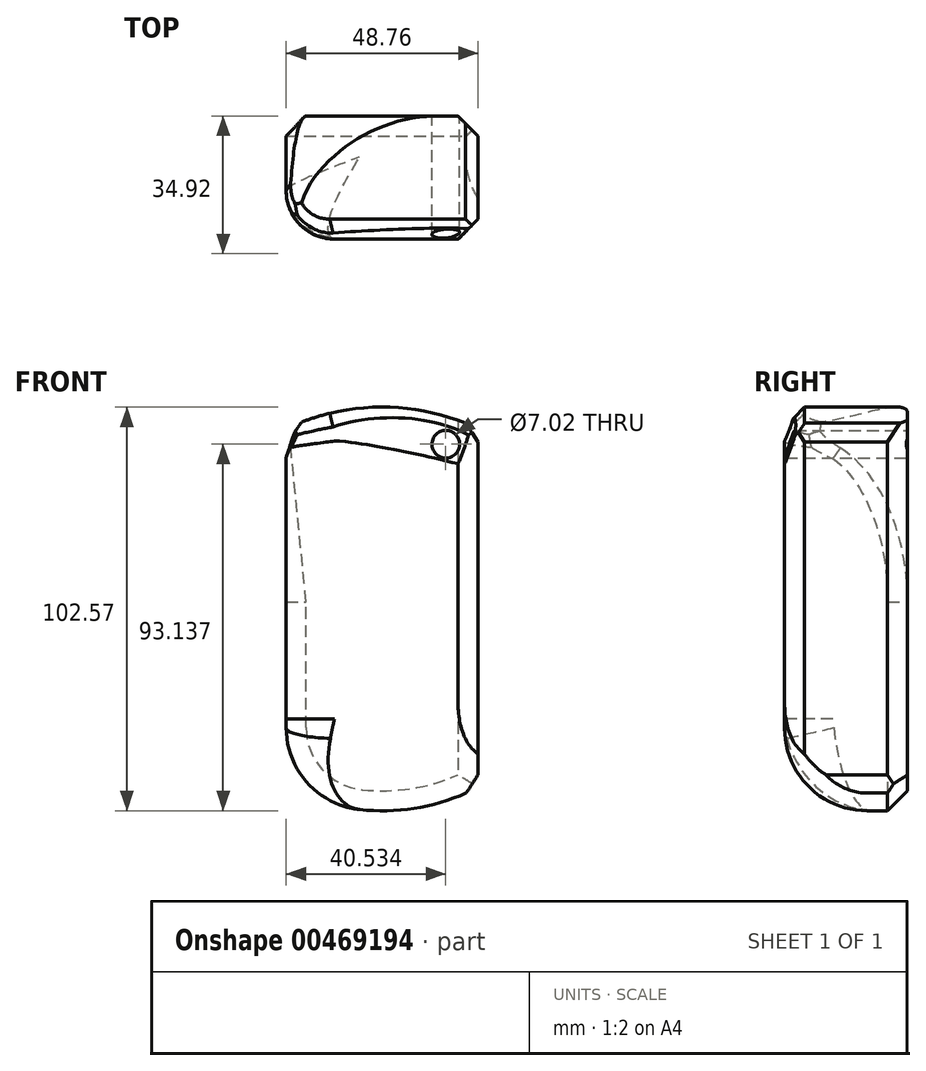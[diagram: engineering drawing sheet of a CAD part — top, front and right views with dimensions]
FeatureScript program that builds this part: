
annotation { "Feature Type Name" : "Feature", "Feature Type Description" : "" }
export const myFeature = defineFeature(function(context is Context, id is Id, definition is map)
    precondition{}
    {
        {
            var Q0;
            Q0=qCreatedBy(makeId("Front.planeOp"),FACE);
            var sketch = newSketch(context, id + "F0", { "sketchPlane" : qUnion([Q0])});
            skLineSegment(sketch, "E0", {"start": v(-24.38, 31.33) * mm, "end": v(-24.38, -48) * mm});
            skLineSegment(sketch, "E1", {"start": v(24.38, 31.33) * mm, "end": v(24.38, -48) * mm});
            skArc(sketch, "E2", {"start": v(-24.38, -48) * mm, "mid": v(0, -53.97) * mm, "end": v(24.38, -48) * mm});
            skArc(sketch, "E3", {"start": v(-24.38, 31.33) * mm, "mid": v(0, 29.36) * mm, "end": v(24.38, 31.33) * mm});
            skLineSegment(sketch, "E4", {"start": v(-24.38, 31.33) * mm, "end": v(-24.38, 36.08) * mm});
            skLineSegment(sketch, "E5", {"start": v(-24.38, 36.08) * mm, "end": v(24.38, 36.08) * mm});
            skLineSegment(sketch, "E6", {"start": v(24.38, 36.08) * mm, "end": v(24.38, 31.33) * mm});
            skLineSegment(sketch, "E7", {"start": v(-24.38, 36.08) * mm, "end": v(-24.38, 43.1) * mm});
            skLineSegment(sketch, "E8", {"start": v(-24.38, 43.1) * mm, "end": v(24.38, 43.1) * mm});
            skLineSegment(sketch, "E9", {"start": v(24.38, 43.1) * mm, "end": v(24.38, 36.08) * mm});
            skArc(sketch, "E10", {"start": v(24.38, 43.1) * mm, "mid": v(0, 48.6) * mm, "end": v(-24.38, 43.1) * mm});
            skCircle(sketch, "E11", {"center": v(16.15, 39.17) * mm, "radius": 3.51 * mm});
            skSolve(sketch);
        }
        {
            var Q0;
            Q0=makeQuery(id+"F0.imprint","IMPRINT",FACE,{"disambiguationData":[TD([[makeQuery(id+"F0.imprint","IMPRINT",EDGE,{"derivedFrom":sQuery(id+"F0.wireOp",EDGE,"E0")}),1.0]])]});
            var Q1;
            {var subQ0=sQuery(id+"F0.wireOp",EDGE,"E7");Q1=makeQuery(id+"F0.imprint","IMPRINT",FACE,{"disambiguationData":[TD([[makeQuery(id+"F0.imprint","IMPRINT",EDGE,{"derivedFrom":subQ0}),-1.0]])]});}
            var Q2;
            Q2=makeQuery(id+"F0.imprint","IMPRINT",FACE,{"disambiguationData":[TD([[makeQuery(id+"F0.imprint","IMPRINT",EDGE,{"derivedFrom":sQuery(id+"F0.wireOp",EDGE,"E8")}),1.0]])]});
            var Q3;
            Q3=makeQuery(id+"F0.imprint","IMPRINT",FACE,{"disambiguationData":[TD([[makeQuery(id+"F0.imprint","IMPRINT",EDGE,{"derivedFrom":sQuery(id+"F0.wireOp",EDGE,"E3")}),1.0]])]});
            extrude(context, id + "F1", {"entities" : qUnion([Q0, Q1, Q2, Q3]), "depth" : 31.24 * mm});
        }
        {
            var Q0;
            Q0=makeQuery(id+"F1.opExtrude","CAP_EDGE",EDGE,{"disambiguationData":[OSD([sQuery(id+"F0.wireOp",EDGE,"E0"),sQuery(id+"F0.wireOp",EDGE,"E4"),sQuery(id+"F0.wireOp",EDGE,"E7")])],"isStart":false});
            fillet(context, id + "F2", {"entities" : qUnion([Q0]), "radius" : 12.26 * mm, "tangentPropagation" : true, "allowEdgeOverflow" : false});
        }
        {
            var Q0;
            Q0=makeQuery(id+"F1.opExtrude","SWEPT_FACE",FACE,{"disambiguationData":[OSD([sQuery(id+"F0.wireOp",EDGE,"E1"),sQuery(id+"F0.wireOp",EDGE,"E6"),sQuery(id+"F0.wireOp",EDGE,"E9")])]});
            chamfer(context, id + "F3", {"entities" : qUnion([Q0]), "width" : 5.08 * mm, "tangentPropagation" : true});
        }
        {
            var Q0;
            Q0=makeQuery(id+"F1.opExtrude","SWEPT_EDGE",EDGE,{"disambiguationData":[OSD([sQuery(id+"F0.wireOp",EDGE,"E7"),sQuery(id+"F0.wireOp",EDGE,"E8"),sQuery(id+"F0.wireOp",EDGE,"E10")])]});
            chamfer(context, id + "F4", {"entities" : qUnion([Q0]), "width" : 5.08 * mm, "tangentPropagation" : true});
        }
        {
            var Q0;
            Q0=makeQuery(id+"F1.opExtrude","SWEPT_EDGE",EDGE,{"disambiguationData":[OSD([sQuery(id+"F0.wireOp",EDGE,"E0"),sQuery(id+"F0.wireOp",EDGE,"E2")])]});
            fillet(context, id + "F5", {"entities" : qUnion([Q0]), "radius" : 20.94 * mm, "tangentPropagation" : true, "allowEdgeOverflow" : false});
        }
        {
            var Q0;
            {var subQ0=sQuery(id+"F0.wireOp",EDGE,"E10");var subQ1=sQuery(id+"F0.wireOp",EDGE,"E7");Q0=makeQuery(id+"F4.opChamfer","BLEND_EDGE",EDGE,{"blendedFrom":[makeQuery(id+"F1.opExtrude","SWEPT_EDGE",EDGE,{"disambiguationData":[OSD([subQ1,sQuery(id+"F0.wireOp",EDGE,"E8"),subQ0])]}),makeQuery(id+"F1.opExtrude","CAP_FACE",FACE,{"disambiguationData":[OSD([sQuery(id+"F0.wireOp",EDGE,"E0"),sQuery(id+"F0.wireOp",EDGE,"E1"),sQuery(id+"F0.wireOp",EDGE,"E2"),sQuery(id+"F0.wireOp",EDGE,"E4"),sQuery(id+"F0.wireOp",EDGE,"E6"),subQ1,sQuery(id+"F0.wireOp",EDGE,"E9"),subQ0,sQuery(id+"F0.wireOp",EDGE,"E11")])],"isStart":true})],"blendedInto":[makeQuery(id+"F1.opExtrude","CAP_FACE",FACE,{"disambiguationData":[OSD([sQuery(id+"F0.wireOp",EDGE,"E0"),sQuery(id+"F0.wireOp",EDGE,"E1"),sQuery(id+"F0.wireOp",EDGE,"E2"),sQuery(id+"F0.wireOp",EDGE,"E4"),sQuery(id+"F0.wireOp",EDGE,"E6"),subQ1,sQuery(id+"F0.wireOp",EDGE,"E9"),subQ0,sQuery(id+"F0.wireOp",EDGE,"E11")])],"isStart":true})]});}
            fillet(context, id + "F6", {"entities" : qUnion([Q0]), "radius" : 26.98 * mm, "tangentPropagation" : true, "allowEdgeOverflow" : false});
        }
        {
            var Q0;
            {var subQ0=sQuery(id+"F0.wireOp",EDGE,"E7");var subQ1=sQuery(id+"F0.wireOp",EDGE,"E4");var subQ2=sQuery(id+"F0.wireOp",EDGE,"E0");Q0=makeQuery(id+"F4.opChamfer","BLEND_EDGE",EDGE,{"blendedFrom":[makeQuery(id+"F2.opFillet","BLEND_EDGE",EDGE,{"blendedFrom":[makeQuery(id+"F1.opExtrude","CAP_EDGE",EDGE,{"disambiguationData":[OSD([subQ2,subQ1,subQ0])],"isStart":false}),makeQuery(id+"F1.opExtrude","SWEPT_FACE",FACE,{"disambiguationData":[OSD([sQuery(id+"F0.wireOp",EDGE,"E10")])]})],"blendedInto":[makeQuery(id+"F1.opExtrude","SWEPT_FACE",FACE,{"disambiguationData":[OSD([sQuery(id+"F0.wireOp",EDGE,"E10")])]})]}),makeQuery(id+"F2.opFillet","BLEND_FACE",FACE,{"disambiguationData":[OSD([subQ2,subQ1,subQ0])]})],"blendedInto":[makeQuery(id+"F2.opFillet","BLEND_FACE",FACE,{"disambiguationData":[OSD([subQ2,subQ1,subQ0])]})]});}
            var Q1;
            {var subQ0=sQuery(id+"F0.wireOp",EDGE,"E7");var subQ1=sQuery(id+"F0.wireOp",EDGE,"E4");var subQ2=sQuery(id+"F0.wireOp",EDGE,"E0");Q1=makeQuery(id+"F2.opFillet","BLEND_EDGE",EDGE,{"blendedFrom":[makeQuery(id+"F1.opExtrude","CAP_EDGE",EDGE,{"disambiguationData":[OSD([subQ2,subQ1,subQ0])],"isStart":false}),makeQuery(id+"F1.opExtrude","SWEPT_FACE",FACE,{"disambiguationData":[OSD([subQ2,subQ1,subQ0])]})],"blendedInto":[makeQuery(id+"F1.opExtrude","SWEPT_FACE",FACE,{"disambiguationData":[OSD([subQ2,subQ1,subQ0])]})]});}
            var Q2;
            Q2=makeQuery(id+"F2.opFillet","BLEND_FACE",FACE,{"disambiguationData":[OSD([sQuery(id+"F0.wireOp",EDGE,"E0"),sQuery(id+"F0.wireOp",EDGE,"E4"),sQuery(id+"F0.wireOp",EDGE,"E7")])]});
            var Q3;
            Q3=makeQuery(id+"F1.opExtrude","SWEPT_FACE",FACE,{"disambiguationData":[OSD([sQuery(id+"F0.wireOp",EDGE,"E0"),sQuery(id+"F0.wireOp",EDGE,"E4"),sQuery(id+"F0.wireOp",EDGE,"E7")])]});
            chamfer(context, id + "F7", {"entities" : qUnion([Q0, Q1, Q2, Q3]), "width" : 5.08 * mm, "tangentPropagation" : true});
        }
    });
